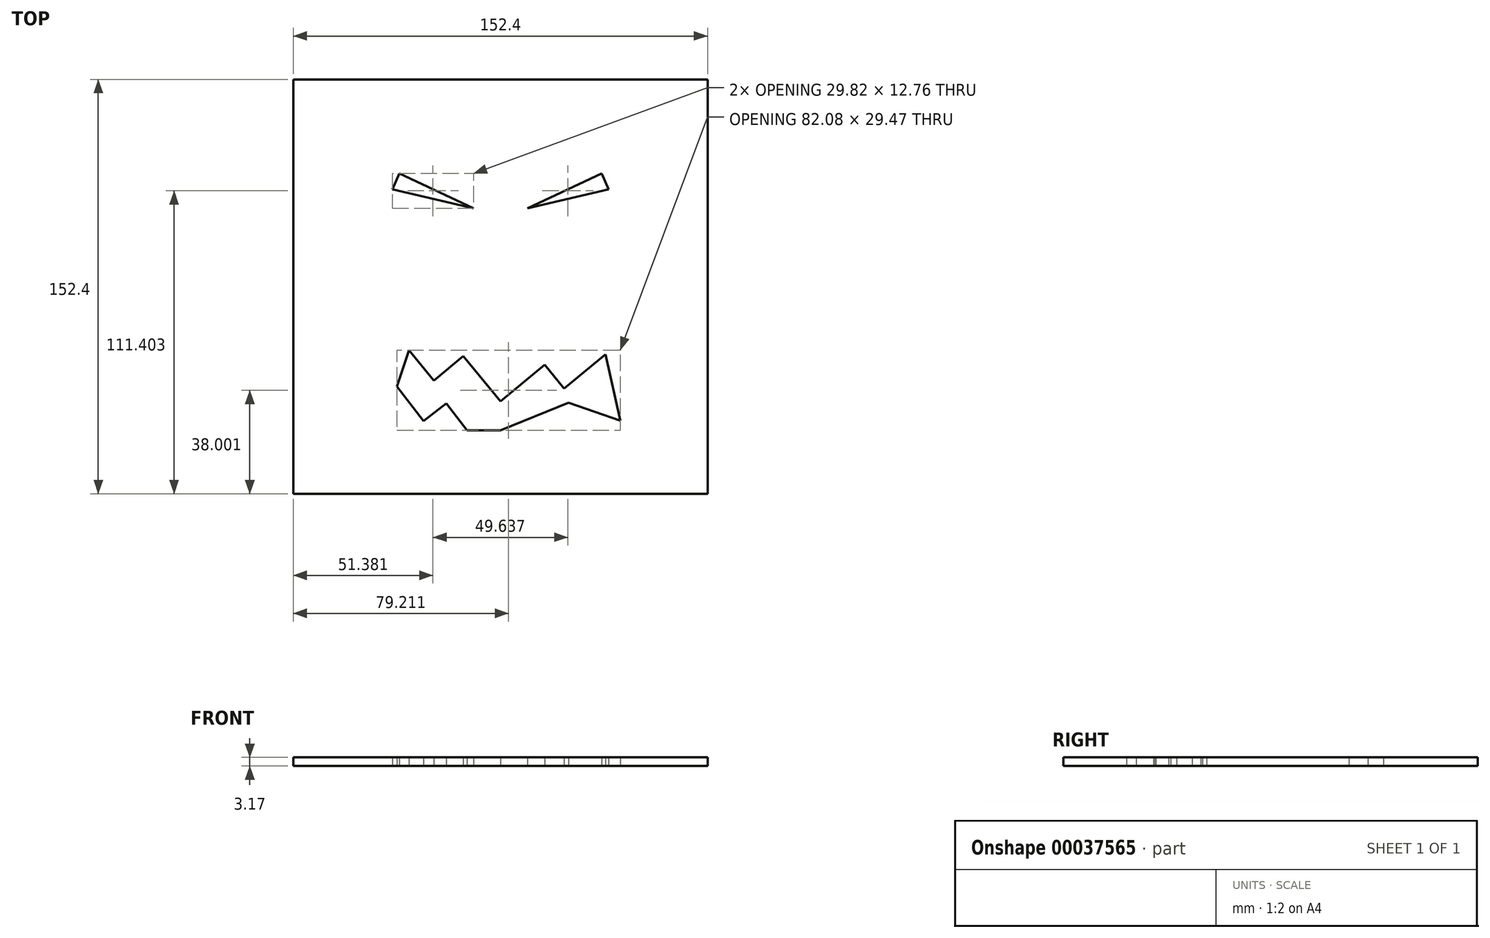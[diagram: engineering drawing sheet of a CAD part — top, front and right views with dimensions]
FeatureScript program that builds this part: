
annotation { "Feature Type Name" : "Feature", "Feature Type Description" : "" }
export const myFeature = defineFeature(function(context is Context, id is Id, definition is map)
    precondition{}
    {
        {
            var Q0;
            Q0=qCreatedBy(makeId("Top.planeOp"),FACE);
            var sketch = newSketch(context, id + "F0", { "sketchPlane" : qUnion([Q0])});
            skPoint(sketch, "E0.rect.middle", {"position": v(0, 0) * mm});
            skLineSegment(sketch, "E1", {"start": v(-37.24, 41.58) * mm, "end": v(-9.9, 28.82) * mm});
            skLineSegment(sketch, "E2", {"start": v(-9.9, 28.82) * mm, "end": v(-39.73, 35.78) * mm});
            skLineSegment(sketch, "E3", {"start": v(0, 0) * mm, "end": v(0, 75.48) * mm, "construction": true});
            skLineSegment(sketch, "E4.MirrorCS", {"start": v(9.9, 28.82) * mm, "end": v(39.73, 35.78) * mm});
            skLineSegment(sketch, "E5.MirrorCS", {"start": v(37.24, 41.58) * mm, "end": v(9.9, 28.82) * mm});
            skLineSegment(sketch, "E6", {"start": v(-39.73, 35.78) * mm, "end": v(-37.24, 41.58) * mm});
            skLineSegment(sketch, "E7.MirrorCS", {"start": v(39.73, 35.78) * mm, "end": v(37.24, 41.58) * mm});
            skLineSegment(sketch, "E8", {"start": v(-33.61, -23.46) * mm, "end": v(-24.5, -34.54) * mm});
            skLineSegment(sketch, "E9", {"start": v(-24.5, -34.54) * mm, "end": v(-13.66, -25.61) * mm});
            skLineSegment(sketch, "E10", {"start": v(-13.66, -25.61) * mm, "end": v(0, -42.2) * mm});
            skLineSegment(sketch, "E11", {"start": v(0, -42.2) * mm, "end": v(16.27, -28.8) * mm});
            skLineSegment(sketch, "E12", {"start": v(16.27, -28.8) * mm, "end": v(23.42, -37.48) * mm});
            skLineSegment(sketch, "E13", {"start": v(23.42, -37.48) * mm, "end": v(38.6, -24.98) * mm});
            skLineSegment(sketch, "E14", {"start": v(38.6, -24.98) * mm, "end": v(44.05, -49.35) * mm});
            skLineSegment(sketch, "E15", {"start": v(44.05, -49.35) * mm, "end": v(25, -42.68) * mm});
            skLineSegment(sketch, "E16", {"start": v(25, -42.68) * mm, "end": v(0, -52.93) * mm});
            skLineSegment(sketch, "E17", {"start": v(0, -52.93) * mm, "end": v(-12.28, -52.93) * mm});
            skLineSegment(sketch, "E18", {"start": v(-12.28, -52.93) * mm, "end": v(-19.94, -43) * mm});
            skLineSegment(sketch, "E19", {"start": v(-19.94, -43) * mm, "end": v(-28.24, -49.4) * mm});
            skLineSegment(sketch, "E20", {"start": v(-28.24, -49.4) * mm, "end": v(-38.03, -36.7) * mm});
            skLineSegment(sketch, "E21", {"start": v(-38.03, -36.7) * mm, "end": v(-33.61, -23.46) * mm});
            skLineSegment(sketch, "E22.rect.bottom", {"start": v(76.2, -76.2) * mm, "end": v(-76.2, -76.2) * mm});
            skLineSegment(sketch, "E22.rect.top", {"start": v(76.2, 76.2) * mm, "end": v(-76.2, 76.2) * mm});
            skLineSegment(sketch, "E22.rect.left", {"start": v(76.2, -76.2) * mm, "end": v(76.2, 76.2) * mm});
            skLineSegment(sketch, "E22.rect.right", {"start": v(-76.2, -76.2) * mm, "end": v(-76.2, 76.2) * mm});
            skSolve(sketch);
        }
        {
            var Q0;
            Q0=makeQuery(id+"F0.imprint","IMPRINT",FACE,{"disambiguationData":[TD([[makeQuery(id+"F0.imprint","IMPRINT",EDGE,{"derivedFrom":sQuery(id+"F0.wireOp",EDGE,"E1")}),1.0]])]});
            extrude(context, id + "F1", {"entities" : qUnion([Q0]), "depth" : 3.17 * mm});
        }
    });
